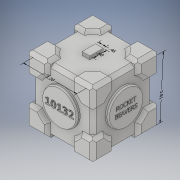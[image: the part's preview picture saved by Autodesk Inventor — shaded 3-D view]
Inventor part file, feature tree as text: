
AUTODESK INVENTOR PART (.ipt)
format: ipt  version: 2018 (Build 220112000, 112)  size: 1,695,232 bytes
history: native  units: in
note: dims shown in document units (in); Inventor stores cm internally (conversion verified against a paired STEP export)
features: chamfer x106, sketch x23, extrude x19, fillet x9, other x5, emboss x4
ambient origin geometry x8: Origin, YZ Plane, XZ Plane, XY Plane, X Axis, Y Axis, Z Axis, Center Point
bodies: Solid1 (feature_tree)
feature tree (166):
  other  "Annotations"
  extrude  "Extrusion1"  Depth=4.0in
  extrude  "Extrusion2"  Depth=1.3in
  extrude  "Extrusion3"  Depth=1.3in
  extrude  "Extrusion4"  Depth=1.3in
  extrude  "Extrusion5"  Depth=1.3in
  extrude  "Extrusion6"  Depth=0.2in
  chamfer  "Chamfer42"  Distance=0.2in
  chamfer  "Chamfer43"  Distance=0.2in
  chamfer  "Chamfer44"  Distance=0.2in
  chamfer  "Chamfer45"  Distance=0.2in
  chamfer  "Chamfer46"  Distance=0.2in Angle=45.0deg
  chamfer  "Chamfer47"  Distance=0.2in Angle=45.0deg
  chamfer  "Chamfer48"  Distance=0.2in Angle=45.0deg
  chamfer  "Chamfer49"  Distance=0.2in Angle=45.0deg
  chamfer  "Chamfer50"  Distance=0.2in Angle=45.0deg
  chamfer  "Chamfer51"  Distance=0.2in Angle=45.0deg
  chamfer  "Chamfer52"  Distance=0.2in Angle=45.0deg
  chamfer  "Chamfer53"  Distance=0.2in Angle=45.0deg
  chamfer  "Chamfer54"  Distance=0.2in Angle=45.0deg
  chamfer  "Chamfer55"  Distance=0.2in Angle=45.0deg
  chamfer  "Chamfer56"  Distance=0.2in Angle=45.0deg
  chamfer  "Chamfer57"  Distance=0.2in Angle=45.0deg
  chamfer  "Chamfer58"  Distance=0.2in Angle=45.0deg
  chamfer  "Chamfer59"  Distance=0.2in Angle=45.0deg
  chamfer  "Chamfer60"  Distance=0.2in Angle=45.0deg
  chamfer  "Chamfer61"  Distance=0.2in Angle=45.0deg
  chamfer  "Chamfer62"  Distance=0.2in Angle=45.0deg
  chamfer  "Chamfer63"  Distance=0.2in Angle=45.0deg
  chamfer  "Chamfer64"  Distance=0.2in Angle=45.0deg
  chamfer  "Chamfer65"  Distance=0.2in Angle=45.0deg
  chamfer  "Chamfer66"  Distance=0.2in Angle=45.0deg
  chamfer  "Chamfer67"  Distance=0.2in Angle=45.0deg
  chamfer  "Chamfer68"  Distance=0.2in Angle=45.0deg
  chamfer  "Chamfer69"  Distance=0.2in Angle=45.0deg
  chamfer  "Chamfer70"  Distance=0.2in Angle=45.0deg
  chamfer  "Chamfer71"  Distance=0.2in Angle=45.0deg
  chamfer  "Chamfer72"  Distance=0.2in Angle=45.0deg
  chamfer  "Chamfer73"  Distance=0.2in Angle=45.0deg
  chamfer  "Chamfer74"  Distance=0.2in Angle=45.0deg
  chamfer  "Chamfer75"  Distance=0.2in Angle=45.0deg
  chamfer  "Chamfer76"  Distance=0.2in Angle=45.0deg
  chamfer  "Chamfer77"  Distance=0.2in Angle=45.0deg
  chamfer  "Chamfer78"  Distance=0.2in Angle=45.0deg
  chamfer  "Chamfer79"  Distance=0.2in Angle=45.0deg
  chamfer  "Chamfer80"  Distance=0.2in Angle=45.0deg
  chamfer  "Chamfer81"  Distance=0.2in Angle=45.0deg
  chamfer  "Chamfer82"  Distance=0.2in Angle=45.0deg
  chamfer  "Chamfer83"  Distance=0.2in Angle=45.0deg
  chamfer  "Chamfer84"  Distance=0.2in Angle=45.0deg
  chamfer  "Chamfer85"  Distance=0.2in Angle=45.0deg
  chamfer  "Chamfer86"  Distance=0.2in Angle=45.0deg
  chamfer  "Chamfer87"  Distance=0.2in Angle=45.0deg
  chamfer  "Chamfer88"  Distance=0.2in Angle=45.0deg
  chamfer  "Chamfer89"  Distance=0.2in Angle=45.0deg
  chamfer  "Chamfer90"  Distance=0.2in Angle=45.0deg
  chamfer  "Chamfer91"  Distance=0.2in Angle=45.0deg
  chamfer  "Chamfer92"  Distance=0.2in Angle=45.0deg
  chamfer  "Chamfer93"  Distance=0.2in Angle=45.0deg
  chamfer  "Chamfer94"  Distance=0.2in Angle=45.0deg
  chamfer  "Chamfer95"  Distance=0.2in Angle=45.0deg
  chamfer  "Chamfer96"  Distance=0.2in Angle=45.0deg
  chamfer  "Chamfer97"  Distance=0.2in Angle=45.0deg
  chamfer  "Chamfer98"  Distance=0.2in Angle=45.0deg
  chamfer  "Chamfer99"  Distance=0.2in Angle=45.0deg
  chamfer  "Chamfer100"  Distance=0.2in Angle=45.0deg
  chamfer  "Chamfer101"  Distance=0.2in Angle=45.0deg
  chamfer  "Chamfer102"  Distance=0.2in Angle=45.0deg
  chamfer  "Chamfer103"  Distance=0.2in Angle=45.0deg
  chamfer  "Chamfer104"  Distance=0.2in Angle=45.0deg
  chamfer  "Chamfer105"  Distance=0.2in Angle=45.0deg
  chamfer  "Chamfer106"  Distance=0.2in Angle=45.0deg
  chamfer  "Chamfer107"  Distance=0.2in Angle=45.0deg
  chamfer  "Chamfer108"  Distance=0.2in Angle=45.0deg
  chamfer  "Chamfer109"  Distance=0.2in Angle=45.0deg
  chamfer  "Chamfer110"  Distance=0.2in Angle=45.0deg
  chamfer  "Chamfer111"  Distance=0.2in Angle=45.0deg
  chamfer  "Chamfer112"  Distance=0.2in Angle=45.0deg
  chamfer  "Chamfer113"  Distance=0.2in Angle=45.0deg
  chamfer  "Chamfer114"  Distance=0.2in Angle=45.0deg
  chamfer  "Chamfer115"  Distance=0.2in Angle=45.0deg
  chamfer  "Chamfer116"  Distance=0.2in Angle=45.0deg
  chamfer  "Chamfer117"  Distance=0.2in Angle=45.0deg
  extrude  "Extrusion7"  Depth=0.2in TaperAngle=45.0deg
  extrude  "Extrusion8"  Depth=0.2in TaperAngle=45.0deg
  extrude  "Extrusion9"  Depth=0.2in TaperAngle=0.0deg
  extrude  "Extrusion10"  Depth=0.2in TaperAngle=0.0deg
  chamfer  "Chamfer118"  Distance=0.2in
  chamfer  "Chamfer119"  Distance=0.2in
  chamfer  "Chamfer120"  Distance=0.2in Angle=45.0deg
  chamfer  "Chamfer121"  Distance=0.2in Angle=45.0deg
  chamfer  "Chamfer122"  Distance=0.2in Angle=45.0deg
  chamfer  "Chamfer123"  Distance=0.2in Angle=45.0deg
  chamfer  "Chamfer124"  Distance=0.2in Angle=45.0deg
  chamfer  "Chamfer125"  Distance=0.2in Angle=45.0deg
  chamfer  "Chamfer126"  Distance=0.2in Angle=45.0deg
  chamfer  "Chamfer127"  Distance=0.2in Angle=45.0deg
  chamfer  "Chamfer128"  Distance=0.2in Angle=45.0deg
  chamfer  "Chamfer129"  Distance=0.2in Angle=45.0deg
  chamfer  "Chamfer130"  Distance=0.2in Angle=45.0deg
  chamfer  "Chamfer131"  Distance=0.2in Angle=45.0deg
  chamfer  "Chamfer132"  Distance=0.2in Angle=45.0deg
  chamfer  "Chamfer133"  Distance=0.2in Angle=45.0deg
  extrude  "Extrusion11"  Depth=0.2in TaperAngle=45.0deg
  chamfer  "Chamfer134"  Distance=0.2in
  chamfer  "Chamfer135"  Distance=0.2in Angle=45.0deg
  chamfer  "Chamfer136"  Distance=0.2in Angle=45.0deg
  chamfer  "Chamfer137"  Distance=0.2in Angle=45.0deg
  extrude  "Extrusion12"  Depth=0.2in
  sketch  "Sketch16"  dims[d379=2.8in d380=0.2in d381=0.0in]
  sketch  "Sketch17"  dims[d382=2.8in d383=0.2in d384=0.0in]
  extrude  "Extrusion13"  Depth=0.2in
  extrude  "Extrusion14"  Depth=2.1in
  extrude  "Extrusion15"  Depth=0.2in TaperAngle=0.0deg
  chamfer  "Chamfer138"  Distance=0.2in
  chamfer  "Chamfer139"  Distance=0.1in Angle=45.0deg
  chamfer  "Chamfer140"  Distance=0.1in Angle=45.0deg
  chamfer  "Chamfer141"  Distance=0.1in Angle=45.0deg
  extrude  "Extrusion16"  Depth=0.2in
  extrude  "Extrusion17"  Depth=0.46in TaperAngle=0.0deg
  chamfer  "Chamfer142"  Distance=1.8in
  chamfer  "Chamfer143"  Distance=1.0in
  fillet  "Fillet1"  Radius=0.8in
  fillet  "Fillet2"  Radius=0.8in
  fillet  "Fillet3"  Radius=1.1in
  fillet  "Fillet4"  Radius=1.1in
  fillet  "Fillet5"  Radius=0.1in
  fillet  "Fillet6"  Radius=0.1in
  fillet  "Fillet7"  Radius=0.1in
  fillet  "Fillet8"  Radius=0.1in
  emboss  "Emboss1"
  emboss  "Emboss2"
  emboss  "Emboss3"
  emboss  "Emboss4"
  extrude  "Extrusion18"  Depth=0.1in
  chamfer  "Chamfer144"  Distance=0.1in
  chamfer  "Chamfer145"  Distance=0.2in
  chamfer  "Chamfer146"  Distance=0.2in
  chamfer  "Chamfer147"  Distance=0.2in
  fillet  "Fillet9"  Radius=0.2in
  extrude  "Extrusion19"  Depth=0.46in
  sketch  "Sketch1"  dims[d0=4.0in d1=4.0in]
  sketch  "Sketch2"  dims[d2=4.0in d3=0.0in d4=1.3in]
  sketch  "Sketch3"  dims[d5=1.3in d6=1.3in]
  sketch  "Sketch4"  dims[d7=1.3in d8=1.3in]
  sketch  "Sketch5"  dims[d9=1.3in d10=1.3in]
  sketch  "Sketch6"  dims[d11=0.2in d12=0.0in d13=1.3in]
  sketch  "Sketch9"  dims[d14=1.3in]
  sketch  "Sketch11"  dims[d15=1.3in]
  sketch  "Sketch12"  dims[d16=1.3in d17=0.2in d18=0.0in d19=0.2in d20=0.0in d21=0.2in d22=0.0in d23=0.2in d24=0.0in d148=0.2in d149=0.2in d150=45.0deg d151=0.2in d152=0.2in d153=45.0deg d154=0.2in d155=0.2in d156=45.0deg d157=0.2in d158=0.2in d159=45.0deg d160=0.2in d161=0.2in d162=45.0deg d163=0.2in d164=0.2in d165=45.0deg d166=0.2in d167=0.2in d168=45.0deg d169=0.2in d170=0.2in d171=45.0deg d172=0.2in d173=0.2in d174=45.0deg d175=0.2in d176=0.2in d177=45.0deg d178=0.2in d179=0.2in d180=45.0deg d181=0.2in d182=0.2in d183=45.0deg d184=0.2in d185=0.2in d186=45.0deg d187=0.2in d188=0.2in d189=45.0deg d190=0.2in d191=0.2in d192=45.0deg d193=0.2in d194=0.2in d195=45.0deg d196=0.2in d197=0.2in d198=45.0deg d199=0.2in d200=0.2in d201=45.0deg d202=0.2in d203=0.2in d204=45.0deg d205=0.2in d206=0.2in d207=45.0deg d208=0.2in d209=0.2in d210=45.0deg d211=0.2in d212=0.2in d213=45.0deg d214=0.2in d215=0.2in d216=45.0deg d217=0.2in d218=0.2in d219=45.0deg d220=0.2in d221=0.2in d222=45.0deg d223=0.2in d224=0.2in d225=45.0deg d226=0.2in d227=0.2in d228=45.0deg d229=0.2in d230=0.2in d231=45.0deg d232=0.2in d233=0.2in d234=45.0deg d235=0.2in d236=0.2in d237=45.0deg d238=0.2in d239=0.2in d240=45.0deg d241=0.2in d242=0.2in d243=45.0deg d244=0.2in d245=0.2in d246=45.0deg d247=0.2in d248=0.2in d249=45.0deg d250=0.2in d251=0.2in d252=45.0deg d253=0.2in d254=0.2in d255=45.0deg d256=0.2in d257=0.2in d258=45.0deg d259=0.2in d260=0.2in d261=45.0deg d262=0.2in d263=0.2in d264=45.0deg d265=0.2in d266=0.2in d267=45.0deg d268=0.2in d269=0.2in d270=45.0deg d271=0.2in d272=0.2in d273=45.0deg d274=0.2in d275=0.2in d276=45.0deg d277=0.2in d278=0.2in d279=45.0deg d280=0.2in d281=0.2in d282=45.0deg d283=0.2in d284=0.2in d285=45.0deg d286=0.2in d287=0.2in d288=45.0deg d289=0.2in d290=0.2in d291=45.0deg d292=0.2in d293=0.2in d294=45.0deg d295=0.2in d296=0.2in d297=45.0deg d298=0.2in d299=0.2in d300=45.0deg d301=0.2in d302=0.2in d303=45.0deg d304=0.2in d305=0.2in d306=45.0deg d307=0.2in d308=0.2in d309=45.0deg d310=0.2in d311=0.2in d312=45.0deg d313=0.2in d314=0.2in d315=45.0deg d316=0.2in d317=0.2in d318=45.0deg d319=0.2in d320=0.2in d321=45.0deg d322=0.2in d323=0.2in d324=45.0deg d325=0.2in d326=0.2in d327=45.0deg d328=0.2in d329=0.2in d330=45.0deg d331=0.2in d332=0.2in d333=45.0deg d334=0.2in d335=0.2in d336=45.0deg d337=0.2in d338=0.2in d339=45.0deg d340=0.2in d341=0.2in d342=45.0deg d343=0.2in d344=0.2in d345=45.0deg d346=0.2in d347=0.2in d348=45.0deg d349=0.2in d350=0.2in d351=45.0deg d352=0.2in d353=0.2in d354=45.0deg d355=0.2in d356=0.2in d357=45.0deg d358=0.2in d359=0.2in d360=45.0deg d361=0.2in d362=0.2in d363=45.0deg]
  sketch  "Sketch13"  dims[d364=0.2in d365=0.2in d366=45.0deg d367=0.2in d368=0.2in d369=45.0deg]
  sketch  "Sketch14"  dims[d370=0.2in d371=0.2in d372=45.0deg d373=0.2in d374=0.2in d375=45.0deg]
  sketch  "Sketch15"  dims[d376=2.8in d377=0.2in d378=0.0in]
  sketch  "Sketch18"  dims[d385=2.8in d386=0.2in d387=0.0in d388=0.2in d389=0.2in d390=45.0deg d391=0.2in d392=0.2in d393=45.0deg d394=0.2in d395=0.2in d396=45.0deg d397=0.2in d398=0.2in d399=45.0deg d400=0.2in d401=0.2in d402=45.0deg d403=0.2in d404=0.2in d405=45.0deg d406=0.2in d407=0.2in d408=45.0deg d409=0.2in d410=0.2in d411=45.0deg d412=0.2in d413=0.2in d414=45.0deg d415=0.2in d416=0.2in d417=45.0deg d418=0.2in d419=0.2in d420=45.0deg d421=0.2in d422=0.2in d423=45.0deg d424=0.2in d425=0.2in d426=45.0deg d427=0.2in d428=0.2in d429=45.0deg]
  sketch  "Sketch19"  dims[d430=0.2in d431=0.2in d432=45.0deg d433=0.2in d434=0.2in d435=45.0deg]
  sketch  "Sketch20"  dims[d436=2.8in d437=0.2in d438=0.0in d439=0.2in d440=0.2in d441=45.0deg d442=0.2in d443=0.2in d444=45.0deg d445=0.2in d446=0.2in d447=45.0deg]
  sketch  "Sketch21"  dims[d448=0.2in d449=0.2in d450=45.0deg d451=2.1in]
  sketch  "Sketch22"  dims[d452=0.2in d453=0.0in d454=2.1in]
  sketch  "Sketch23"  dims[d455=2.1in d456=2.1in]
  sketch  "Sketch24"  dims[d457=0.2in d458=0.0in d459=0.2in d460=0.0in d461=0.2in d462=0.0in d463=0.05in d464=0.1in d465=45.0deg d466=0.05in d467=0.1in d468=45.0deg d469=0.05in d470=0.1in d471=45.0deg]
  sketch  "Sketch25"  dims[d472=0.05in d473=0.1in d474=45.0deg d475=0.2in]
  sketch  "Sketch26"  dims[d476=0.2in d477=3.0in d478=0.0in d479=1.8in d480=1.0in d481=0.0in d488=0.8in d489=3.0in d490=45.0deg d491=0.8in d492=3.0in d493=45.0deg d494=1.1in d495=1.1in d496=0.1in d497=0.1in d498=0.1in d499=0.1in d500=0.1in d501=0.1in d502=0.2in d503=0.0in d504=0.2in d505=0.0in d506=0.2in d507=0.0in d508=0.2in d509=0.0in d513=0.7in d514=0.7in d515=0.7in d516=0.7in d517=1.2in d518=0.0in d519=1.2in d520=0.15in d521=45.0deg d522=1.2in d523=0.15in d524=45.0deg d525=1.2in d526=0.15in d527=45.0deg d528=1.2in d529=0.15in d530=45.0deg d531=0.1in d537=0.4in d538=0.23in d539=0.8in d540=0.46in d541=0.2in d542=0.0in d546=1.0in d547=3.2in d534=0.2398in d535=0.3315in d536=3.8053in d548=0.1438in d549=0.251in d550=0.8in d551=0.156in d552=0.2976in d553=0.46in d554=0.2502in d555=0.2277in d556=3.2in]
  other  "Linear Dimension 5"
  other  "Linear Dimension 7"
  other  "Linear Dimension 8"
  other  "Linear Dimension 9"
